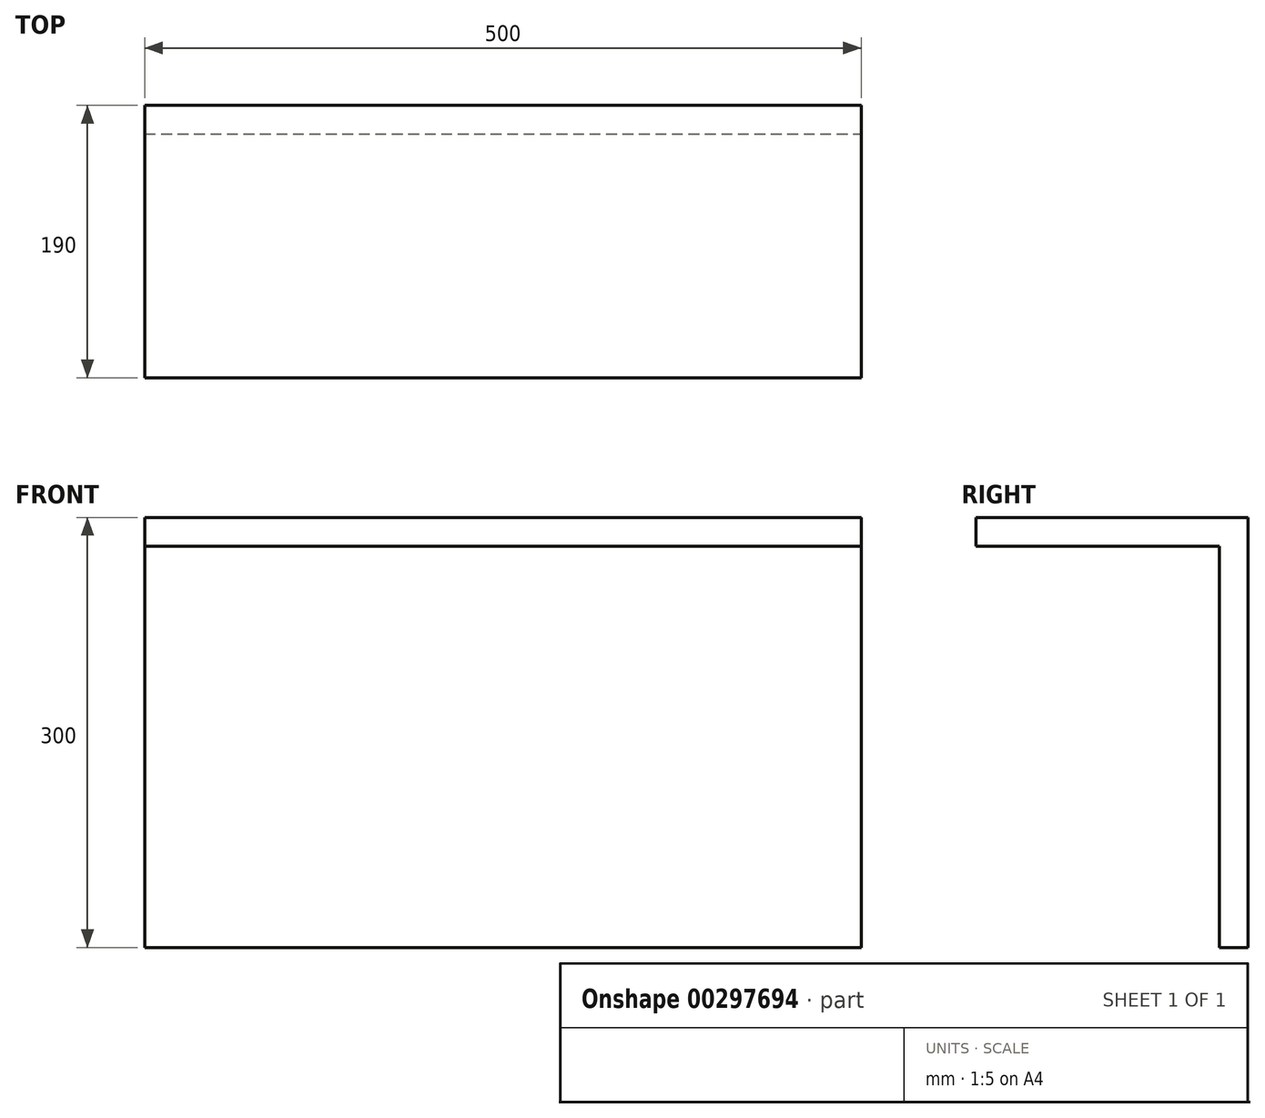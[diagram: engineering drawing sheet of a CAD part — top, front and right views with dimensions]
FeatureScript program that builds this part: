
annotation { "Feature Type Name" : "Feature", "Feature Type Description" : "" }
export const myFeature = defineFeature(function(context is Context, id is Id, definition is map)
    precondition{}
    {
        {
            var Q0;
            Q0=qCreatedBy(makeId("Top.planeOp"),FACE);
            var sketch = newSketch(context, id + "F0", { "sketchPlane" : qUnion([Q0])});
            skLineSegment(sketch, "E0", {"start": v(0, 0) * mm, "end": v(250, 0) * mm, "construction": true});
            skLineSegment(sketch, "E1.bottom", {"start": v(250, 0) * mm, "end": v(-250, 0) * mm});
            skLineSegment(sketch, "E1.top", {"start": v(250, -190) * mm, "end": v(-250, -190) * mm});
            skLineSegment(sketch, "E1.left", {"start": v(250, 0) * mm, "end": v(250, -190) * mm});
            skLineSegment(sketch, "E1.right", {"start": v(-250, 0) * mm, "end": v(-250, -190) * mm});
            skSolve(sketch);
        }
        {
            var Q0;
            Q0=makeQuery(id+"F0.imprint","IMPRINT",FACE,{"disambiguationData":[TD([[makeQuery(id+"F0.imprint","IMPRINT",EDGE,{"derivedFrom":sQuery(id+"F0.wireOp",EDGE,"E1.bottom")}),1.0]])]});
            extrude(context, id + "F1", {"entities" : qUnion([Q0]), "oppositeDirection" : true, "depth" : 20 * mm});
        }
        {
            var Q0;
            Q0=qCreatedBy(makeId("Front.planeOp"),FACE);
            var sketch = newSketch(context, id + "F2", { "sketchPlane" : qUnion([Q0])});
            skLineSegment(sketch, "E2", {"start": v(0, 0) * mm, "end": v(0, -300) * mm, "construction": true});
            skLineSegment(sketch, "E3", {"start": v(0, -300) * mm, "end": v(250, -300) * mm, "construction": true});
            skLineSegment(sketch, "E4", {"start": v(0, 0) * mm, "end": v(-250, 0) * mm, "construction": true});
            skLineSegment(sketch, "E5.bottom", {"start": v(250, -300) * mm, "end": v(-250, -300) * mm});
            skLineSegment(sketch, "E5.top", {"start": v(250, 0) * mm, "end": v(-250, 0) * mm});
            skLineSegment(sketch, "E5.left", {"start": v(250, -300) * mm, "end": v(250, 0) * mm});
            skLineSegment(sketch, "E5.right", {"start": v(-250, -300) * mm, "end": v(-250, 0) * mm});
            skSolve(sketch);
        }
        {
            var Q0;
            Q0=makeQuery(id+"F2.imprint","IMPRINT",FACE,{"disambiguationData":[TD([[makeQuery(id+"F2.imprint","IMPRINT",EDGE,{"derivedFrom":sQuery(id+"F2.wireOp",EDGE,"E5.bottom")}),-1.0]])]});
            extrude(context, id + "F3", {"entities" : qUnion([Q0]), "operationType" : NewBodyOperationType.ADD, "depth" : 20 * mm});
        }
        {
            var Q0;
            Q0=makeQuery(id+"F3.opExtrude","CAP_FACE",FACE,{"disambiguationData":[OSD([sQuery(id+"F2.wireOp",EDGE,"E5.bottom"),sQuery(id+"F2.wireOp",EDGE,"E5.top"),sQuery(id+"F2.wireOp",EDGE,"E5.left"),sQuery(id+"F2.wireOp",EDGE,"E5.right")])],"isStart":false});
            var sketch = newSketch(context, id + "F4", { "sketchPlane" : qUnion([Q0])});
            skLineSegment(sketch, "E6", {"start": v(0, -20) * mm, "end": v(0, -150) * mm, "construction": true});
            skPoint(sketch, "E6.endSnap0", {"position": v(0, -20) * mm});
            skLineSegment(sketch, "E7.bottom", {"start": v(-250, -160) * mm, "end": v(250, -160) * mm});
            skLineSegment(sketch, "E7.top", {"start": v(-250, -140) * mm, "end": v(250, -140) * mm});
            skLineSegment(sketch, "E7.left", {"start": v(-250, -160) * mm, "end": v(-250, -140) * mm});
            skLineSegment(sketch, "E7.right", {"start": v(250, -160) * mm, "end": v(250, -140) * mm});
            skPoint(sketch, "E7.middle", {"position": v(0, -150) * mm});
            skSolve(sketch);
        }
        {
            var Q0;
            Q0=sQuery(id+"F4.wireOp",EDGE,"E7.top");
            var Q1;
            Q1=sQuery(id+"F4.wireOp",EDGE,"E7.bottom");
            var Q2;
            Q2=sQuery(id+"F4.wireOp",EDGE,"E7.left");
            var Q3;
            Q3=sQuery(id+"F4.wireOp",EDGE,"E7.right");
            extrude(context, id + "F5", {"bodyType" : ExtendedToolBodyType.SURFACE, "surfaceEntities" : qUnion([Q0, Q1, Q2, Q3]), "depth" : 170 * mm});
        }
        {
            var Q0;
            {var subQ0=sQuery(id+"F4.wireOp",EDGE,"E7.top");Q0=makeQuery(id+"F4.imprint","IMPRINT",FACE,{"disambiguationData":[TD([[makeQuery(id+"F4.imprint","IMPRINT",EDGE,{"derivedFrom":subQ0}),1.0]])]});}
            var sketch = newSketch(context, id + "F6", { "sketchPlane" : qUnion([Q0])});
            skLineSegment(sketch, "E8", {"start": v(-230, -20) * mm, "end": v(0, -20) * mm, "construction": true});
            skLineSegment(sketch, "E9", {"start": v(0, -20) * mm, "end": v(230, -20) * mm, "construction": true});
            skLineSegment(sketch, "E10.bottom", {"start": v(-230, -20) * mm, "end": v(-250, -20) * mm});
            skLineSegment(sketch, "E10.top", {"start": v(-230, -140) * mm, "end": v(-250, -140) * mm});
            skLineSegment(sketch, "E10.left", {"start": v(-230, -20) * mm, "end": v(-230, -140) * mm});
            skLineSegment(sketch, "E10.right", {"start": v(-250, -20) * mm, "end": v(-250, -140) * mm});
            skLineSegment(sketch, "E11.bottom", {"start": v(230, -20) * mm, "end": v(250, -20) * mm});
            skLineSegment(sketch, "E11.top", {"start": v(230, -140) * mm, "end": v(250, -140) * mm});
            skLineSegment(sketch, "E11.left", {"start": v(230, -20) * mm, "end": v(230, -140) * mm});
            skLineSegment(sketch, "E11.right", {"start": v(250, -20) * mm, "end": v(250, -140) * mm});
            skSolve(sketch);
        }
        {
            var Q0;
            Q0=sQuery(id+"F6.wireOp",EDGE,"E10.right");
            var Q1;
            Q1=sQuery(id+"F6.wireOp",EDGE,"E10.left");
            var Q2;
            Q2=sQuery(id+"F6.wireOp",EDGE,"E10.top");
            var Q3;
            Q3=sQuery(id+"F6.wireOp",EDGE,"E10.bottom");
            var Q4;
            Q4=sQuery(id+"F6.wireOp",EDGE,"E11.left");
            var Q5;
            Q5=sQuery(id+"F6.wireOp",EDGE,"E11.right");
            var Q6;
            Q6=sQuery(id+"F6.wireOp",EDGE,"E11.bottom");
            var Q7;
            Q7=sQuery(id+"F6.wireOp",EDGE,"E11.top");
            extrude(context, id + "F7", {"bodyType" : ExtendedToolBodyType.SURFACE, "surfaceEntities" : qUnion([Q0, Q1, Q2, Q3, Q4, Q5, Q6, Q7]), "depth" : 170 * mm});
        }
        {
            var Q0;
            {var subQ0=sQuery(id+"F4.wireOp",EDGE,"E7.top");Q0=makeQuery(id+"F4.imprint","IMPRINT",FACE,{"disambiguationData":[TD([[makeQuery(id+"F4.imprint","IMPRINT",EDGE,{"derivedFrom":subQ0}),1.0]])]});}
            var sketch = newSketch(context, id + "F8", { "sketchPlane" : qUnion([Q0])});
            skLineSegment(sketch, "E12", {"start": v(-70, -20) * mm, "end": v(0, -20) * mm, "construction": true});
            skLineSegment(sketch, "E13", {"start": v(0, -20) * mm, "end": v(70, -20) * mm, "construction": true});
            skLineSegment(sketch, "E14.bottom", {"start": v(-70, -20) * mm, "end": v(-90, -20) * mm});
            skLineSegment(sketch, "E14.top", {"start": v(-70, -140) * mm, "end": v(-90, -140) * mm});
            skLineSegment(sketch, "E14.left", {"start": v(-70, -20) * mm, "end": v(-70, -140) * mm});
            skLineSegment(sketch, "E14.right", {"start": v(-90, -20) * mm, "end": v(-90, -140) * mm});
            skLineSegment(sketch, "E15.bottom", {"start": v(70, -20) * mm, "end": v(90, -20) * mm});
            skLineSegment(sketch, "E15.top", {"start": v(70, -140) * mm, "end": v(90, -140) * mm});
            skLineSegment(sketch, "E15.left", {"start": v(70, -20) * mm, "end": v(70, -140) * mm});
            skLineSegment(sketch, "E15.right", {"start": v(90, -20) * mm, "end": v(90, -140) * mm});
            skSolve(sketch);
        }
        {
            var Q0;
            Q0=sQuery(id+"F8.wireOp",EDGE,"E14.right");
            var Q1;
            Q1=sQuery(id+"F8.wireOp",EDGE,"E14.left");
            var Q2;
            Q2=sQuery(id+"F8.wireOp",EDGE,"E14.bottom");
            var Q3;
            Q3=sQuery(id+"F8.wireOp",EDGE,"E14.top");
            var Q4;
            Q4=sQuery(id+"F8.wireOp",EDGE,"E15.left");
            var Q5;
            Q5=sQuery(id+"F8.wireOp",EDGE,"E15.right");
            var Q6;
            Q6=sQuery(id+"F8.wireOp",EDGE,"E15.top");
            var Q7;
            Q7=sQuery(id+"F8.wireOp",EDGE,"E15.bottom");
            extrude(context, id + "F9", {"bodyType" : ExtendedToolBodyType.SURFACE, "surfaceEntities" : qUnion([Q0, Q1, Q2, Q3, Q4, Q5, Q6, Q7]), "depth" : 170 * mm});
        }
    });
